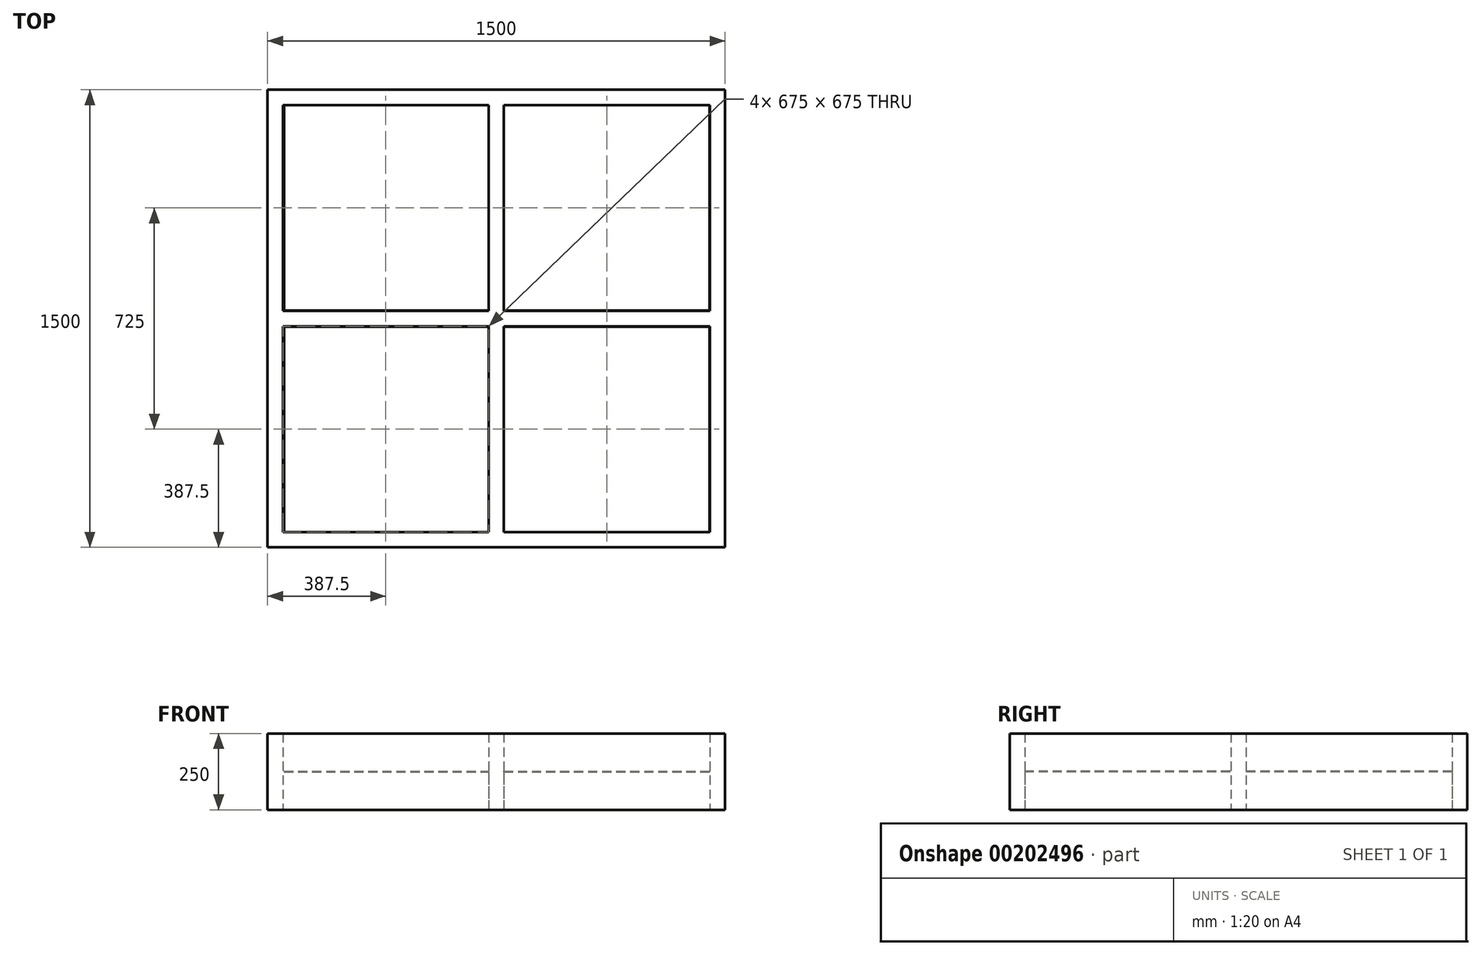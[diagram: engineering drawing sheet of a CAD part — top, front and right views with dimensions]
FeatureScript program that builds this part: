
annotation { "Feature Type Name" : "Feature", "Feature Type Description" : "" }
export const myFeature = defineFeature(function(context is Context, id is Id, definition is map)
    precondition{}
    {
        {
            var Q0;
            Q0=qCreatedBy(makeId("Top.planeOp"),FACE);
            var sketch = newSketch(context, id + "F0", { "sketchPlane" : qUnion([Q0])});
            skLineSegment(sketch, "E0.bottom", {"start": v(750, 750) * mm, "end": v(-750, 750) * mm});
            skLineSegment(sketch, "E0.top", {"start": v(750, -750) * mm, "end": v(-750, -750) * mm});
            skLineSegment(sketch, "E0.left", {"start": v(750, 750) * mm, "end": v(750, -750) * mm});
            skLineSegment(sketch, "E0.right", {"start": v(-750, 750) * mm, "end": v(-750, -750) * mm});
            skPoint(sketch, "E0.middle", {"position": v(0, 0) * mm});
            skLineSegment(sketch, "E1.bottom", {"start": v(-700, 700) * mm, "end": v(-25, 700) * mm});
            skLineSegment(sketch, "E1.top", {"start": v(-700, 25) * mm, "end": v(-25, 25) * mm});
            skLineSegment(sketch, "E1.left", {"start": v(-700, 700) * mm, "end": v(-700, 25) * mm});
            skLineSegment(sketch, "E1.right", {"start": v(-25, 700) * mm, "end": v(-25, 25) * mm});
            skLineSegment(sketch, "E2.bottom", {"start": v(25, 700) * mm, "end": v(700, 700) * mm});
            skLineSegment(sketch, "E2.top", {"start": v(25, 25) * mm, "end": v(700, 25) * mm});
            skLineSegment(sketch, "E2.left", {"start": v(25, 700) * mm, "end": v(25, 25) * mm});
            skLineSegment(sketch, "E2.right", {"start": v(700, 700) * mm, "end": v(700, 25) * mm});
            skLineSegment(sketch, "E3.bottom", {"start": v(-700, -25) * mm, "end": v(-25, -25) * mm});
            skLineSegment(sketch, "E3.top", {"start": v(-700, -700) * mm, "end": v(-25, -700) * mm});
            skLineSegment(sketch, "E3.left", {"start": v(-700, -25) * mm, "end": v(-700, -700) * mm});
            skLineSegment(sketch, "E3.right", {"start": v(-25, -25) * mm, "end": v(-25, -700) * mm});
            skLineSegment(sketch, "E4.bottom", {"start": v(25, -25) * mm, "end": v(700, -25) * mm});
            skLineSegment(sketch, "E4.top", {"start": v(25, -700) * mm, "end": v(700, -700) * mm});
            skLineSegment(sketch, "E4.left", {"start": v(25, -25) * mm, "end": v(25, -700) * mm});
            skLineSegment(sketch, "E4.right", {"start": v(700, -25) * mm, "end": v(700, -700) * mm});
            skSolve(sketch);
        }
        {
            var Q0;
            Q0=makeQuery(id+"F0.imprint","IMPRINT",FACE,{"disambiguationData":[TD([[makeQuery(id+"F0.imprint","IMPRINT",EDGE,{"derivedFrom":sQuery(id+"F0.wireOp",EDGE,"E0.bottom")}),1.0]])]});
            extrude(context, id + "F1", {"entities" : qUnion([Q0]), "endBound" : BoundingType.SYMMETRIC, "depth" : 250 * mm});
        }
        {
            var Q0;
            Q0=qCreatedBy(makeId("Top.planeOp"),FACE);
            var sketch = newSketch(context, id + "F2", { "sketchPlane" : qUnion([Q0])});
            skLineSegment(sketch, "E5.bottom", {"start": v(-695.58, 701.2) * mm, "end": v(-20.58, 701.2) * mm});
            skLineSegment(sketch, "E5.top", {"start": v(-695.58, 26.2) * mm, "end": v(-20.58, 26.2) * mm});
            skLineSegment(sketch, "E5.left", {"start": v(-695.58, 701.2) * mm, "end": v(-695.58, 26.2) * mm});
            skLineSegment(sketch, "E5.right", {"start": v(-20.58, 701.2) * mm, "end": v(-20.58, 26.2) * mm});
            skLineSegment(sketch, "E6.bottom", {"start": v(23.56, 701.2) * mm, "end": v(698.56, 701.2) * mm});
            skLineSegment(sketch, "E6.top", {"start": v(23.56, 26.2) * mm, "end": v(698.56, 26.2) * mm});
            skLineSegment(sketch, "E6.left", {"start": v(23.56, 701.2) * mm, "end": v(23.56, 26.2) * mm});
            skLineSegment(sketch, "E6.right", {"start": v(698.56, 701.2) * mm, "end": v(698.56, 26.2) * mm});
            skLineSegment(sketch, "E7.bottom", {"start": v(-695.58, -27) * mm, "end": v(-20.58, -27) * mm});
            skLineSegment(sketch, "E7.top", {"start": v(-695.58, -702) * mm, "end": v(-20.58, -702) * mm});
            skLineSegment(sketch, "E7.left", {"start": v(-695.58, -27) * mm, "end": v(-695.58, -702) * mm});
            skLineSegment(sketch, "E7.right", {"start": v(-20.58, -27) * mm, "end": v(-20.58, -702) * mm});
            skLineSegment(sketch, "E8.bottom", {"start": v(23.56, -27) * mm, "end": v(698.56, -27) * mm});
            skLineSegment(sketch, "E8.top", {"start": v(23.56, -702) * mm, "end": v(698.56, -702) * mm});
            skLineSegment(sketch, "E8.left", {"start": v(23.56, -27) * mm, "end": v(23.56, -702) * mm});
            skLineSegment(sketch, "E8.right", {"start": v(698.56, -27) * mm, "end": v(698.56, -702) * mm});
            skSolve(sketch);
        }
        {
            var Q0;
            Q0=qSketchRegion(id+"F2",true);
            extrude(context, id + "F3", {"entities" : qUnion([Q0]), "operationType" : NewBodyOperationType.ADD, "endBound" : BoundingType.SYMMETRIC, "depth" : 3 * mm});
        }
    });
